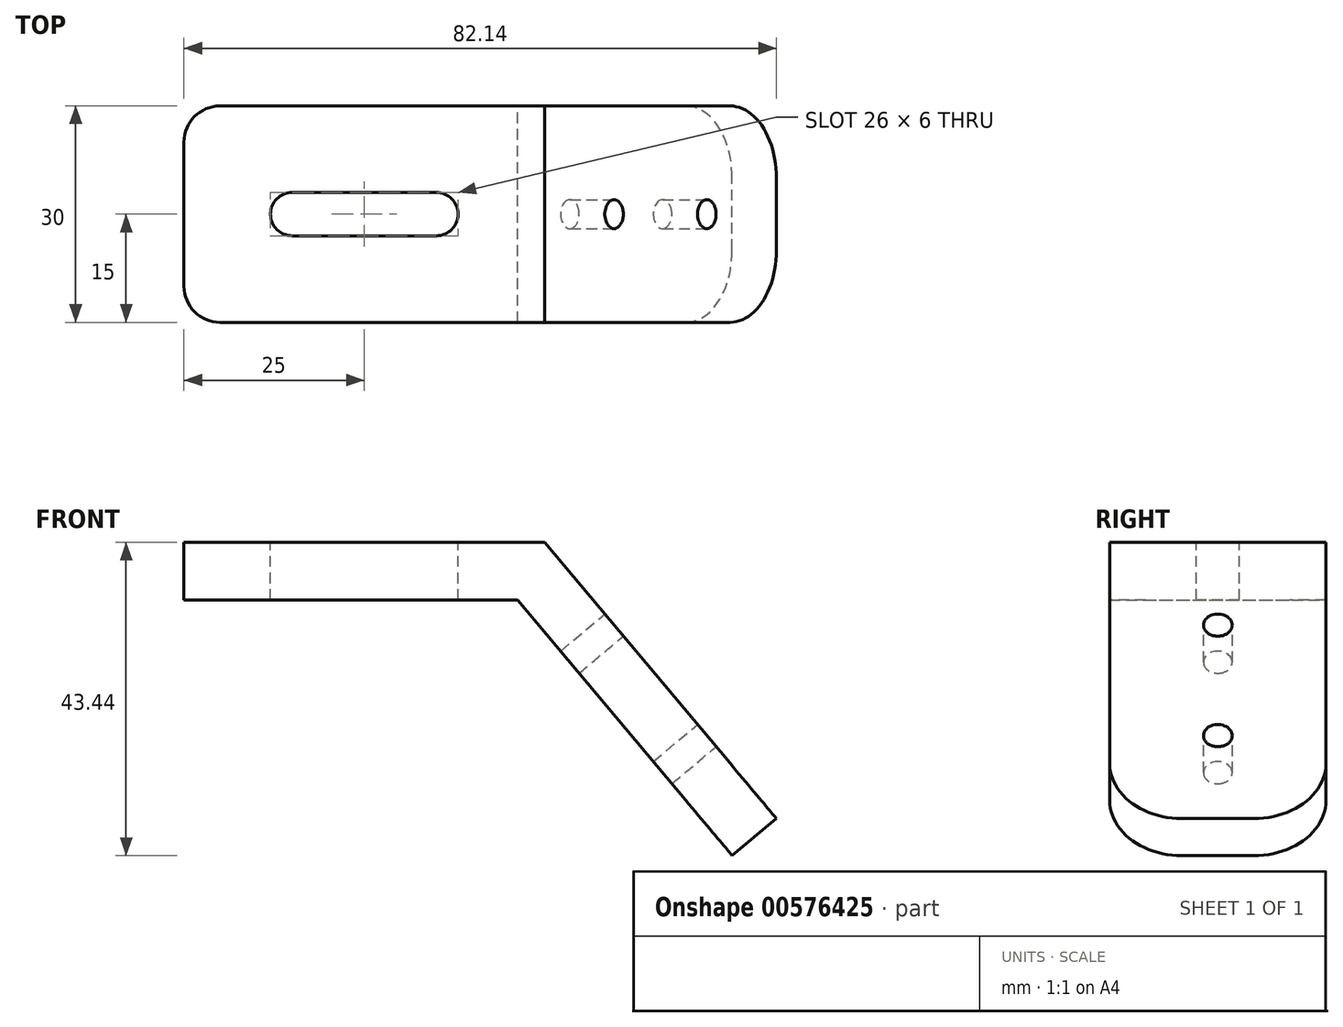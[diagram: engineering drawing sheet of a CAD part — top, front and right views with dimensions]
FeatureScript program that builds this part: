
annotation { "Feature Type Name" : "Feature", "Feature Type Description" : "" }
export const myFeature = defineFeature(function(context is Context, id is Id, definition is map)
    precondition{}
    {
        {
            var Q0;
            Q0=qCreatedBy(makeId("Front.planeOp"),FACE);
            var sketch = newSketch(context, id + "F0", { "sketchPlane" : qUnion([Q0])});
            skLineSegment(sketch, "E0", {"start": v(0, 0) * mm, "end": v(46.27, 0) * mm});
            skLineSegment(sketch, "E1", {"start": v(46.27, 0) * mm, "end": v(76.01, -35.44) * mm});
            skLineSegment(sketch, "E2.0", {"start": v(50, 8) * mm, "end": v(82.14, -30.3) * mm});
            skLineSegment(sketch, "E2.1", {"start": v(0, 8) * mm, "end": v(50, 8) * mm});
            skLineSegment(sketch, "E3", {"start": v(0, 0) * mm, "end": v(0, 8) * mm});
            skLineSegment(sketch, "E4", {"start": v(76.01, -35.44) * mm, "end": v(82.14, -30.3) * mm});
            skSolve(sketch);
        }
        {
            var Q0;
            Q0 = qSketchRegion(id + "F0", true);
            extrude(context, id + "F1", {"entities" : qUnion([Q0]), "endBound" : BoundingType.SYMMETRIC, "depth" : 30 * mm, "offsetDistance" : 25 * mm});
        }
        {
            var Q0;
            Q0=makeQuery(id+"F1.opExtrude","SWEPT_FACE",FACE,{"disambiguationData":[OSD([sQuery(id+"F0.wireOp",EDGE,"E2.1")])]});
            var sketch = newSketch(context, id + "F2", { "sketchPlane" : qUnion([Q0])});
            skLineSegment(sketch, "E5", {"start": v(15, 0) * mm, "end": v(35, 0) * mm});
            skArc(sketch, "E6.0.startCap", {"start": v(15, -3) * mm, "mid": v(12, 0) * mm, "end": v(15, 3) * mm});
            skArc(sketch, "E6.0.endCap", {"start": v(35, 3) * mm, "mid": v(38, 0) * mm, "end": v(35, -3) * mm});
            skLineSegment(sketch, "E6.0.left", {"start": v(15, 3) * mm, "end": v(35, 3) * mm});
            skLineSegment(sketch, "E6.0.right", {"start": v(15, -3) * mm, "end": v(35, -3) * mm});
            skSolve(sketch);
        }
        {
            var Q0;
            Q0 = qSketchRegion(id + "F2", true);
            extrude(context, id + "F3", {"entities" : qUnion([Q0]), "operationType" : NewBodyOperationType.REMOVE, "endBound" : BoundingType.THROUGH_ALL, "oppositeDirection" : true, "depth" : 25 * mm, "offsetDistance" : 25 * mm});
        }
        {
            var Q0;
            Q0=makeQuery(id+"F1.opExtrude","SWEPT_FACE",FACE,{"disambiguationData":[OSD([sQuery(id+"F0.wireOp",EDGE,"E2.0")])]});
            var sketch = newSketch(context, id + "F4", { "sketchPlane" : qUnion([Q0])});
            skPoint(sketch, "E7", {"position": v(0, -41.01) * mm});
            skPoint(sketch, "E7.positionSnap0", {"position": v(0, -26.01) * mm});
            skPoint(sketch, "E8", {"position": v(0, -61.01) * mm});
            skSolve(sketch);
        }
        {
            var Q0;
            Q0=sQuery(id+"F4.wireOp",VERTEX,"E7");
            var Q1;
            Q1=sQuery(id+"F4.wireOp",VERTEX,"E8");
            var Q2;
            Q2=makeQuery(id+"F1.opExtrude","SWEPT_BODY",BODY,{"disambiguationData":[OSD([sQuery(id+"F0.wireOp",EDGE,"E0"),sQuery(id+"F0.wireOp",EDGE,"E1"),sQuery(id+"F0.wireOp",EDGE,"E2.0"),sQuery(id+"F0.wireOp",EDGE,"E2.1"),sQuery(id+"F0.wireOp",EDGE,"E3"),sQuery(id+"F0.wireOp",EDGE,"E4")])]});
            hole(context, id + "F5", {"style" : HoleStyle.SIMPLE, "endStyle" : HoleEndStyle.THROUGH, "holeDiameter" : 4 * mm, "isTappedThrough" : true, "tappedDepth" : 12 * mm, "tapClearance" : 3, "locations" : qUnion([Q0, Q1]), "scope" : qUnion([Q2])});
        }
        {
            var Q0;
            Q0=makeQuery(id+"F1.opExtrude","CAP_EDGE",EDGE,{"disambiguationData":[OSD([sQuery(id+"F0.wireOp",EDGE,"E3")])],"isStart":true});
            var Q1;
            Q1=makeQuery(id+"F1.opExtrude","CAP_EDGE",EDGE,{"disambiguationData":[OSD([sQuery(id+"F0.wireOp",EDGE,"E3")])],"isStart":false});
            fillet(context, id + "F6", {"entities" : qUnion([Q0, Q1]), "radius" : 5 * mm, "tangentPropagation" : true, "allowEdgeOverflow" : false});
        }
        {
            var Q0;
            Q0=makeQuery(id+"F1.opExtrude","CAP_EDGE",EDGE,{"disambiguationData":[OSD([sQuery(id+"F0.wireOp",EDGE,"E4")])],"isStart":false});
            var Q1;
            Q1=makeQuery(id+"F1.opExtrude","CAP_EDGE",EDGE,{"disambiguationData":[OSD([sQuery(id+"F0.wireOp",EDGE,"E4")])],"isStart":true});
            fillet(context, id + "F7", {"entities" : qUnion([Q0, Q1]), "radius" : 10 * mm, "tangentPropagation" : true, "allowEdgeOverflow" : false});
        }
    });
